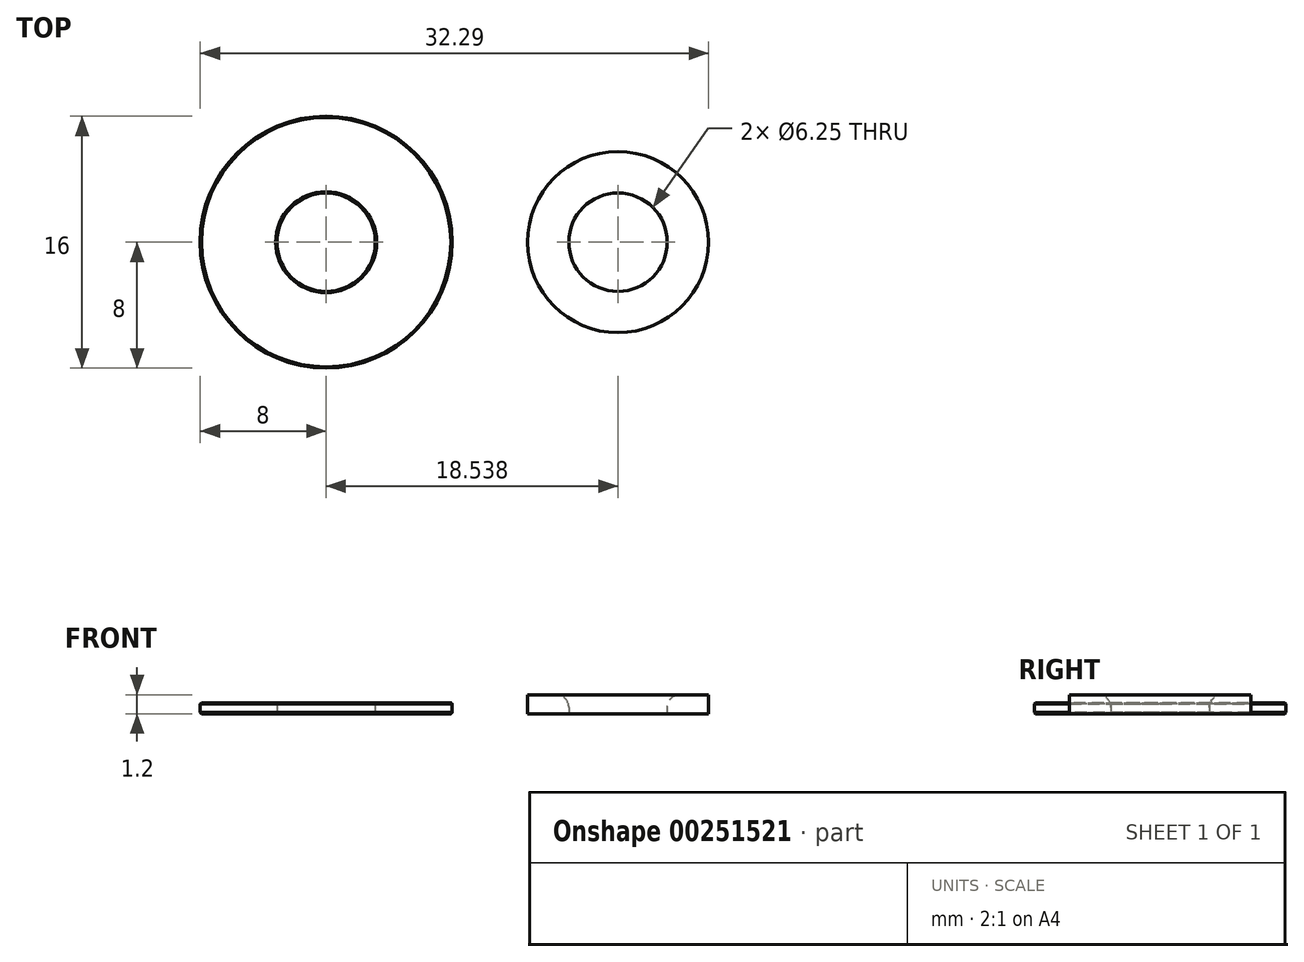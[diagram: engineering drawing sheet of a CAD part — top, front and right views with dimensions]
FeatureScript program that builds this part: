
annotation { "Feature Type Name" : "Feature", "Feature Type Description" : "" }
export const myFeature = defineFeature(function(context is Context, id is Id, definition is map)
    precondition{}
    {
        {
            var Q0;
            Q0=qCreatedBy(makeId("Top.planeOp"),FACE);
            var sketch = newSketch(context, id + "F0", { "sketchPlane" : qUnion([Q0])});
            skCircle(sketch, "E0", {"center": v(0, 0) * mm, "radius": 8 * mm});
            skCircle(sketch, "E1", {"center": v(0, 0) * mm, "radius": 3.12 * mm});
            skCircle(sketch, "E2", {"center": v(18.54, 0) * mm, "radius": 5.75 * mm});
            skCircle(sketch, "E3", {"center": v(18.54, 0) * mm, "radius": 3.12 * mm});
            skSolve(sketch);
        }
        {
            var Q0;
            Q0=makeQuery(id+"F0.imprint","IMPRINT",FACE,{"disambiguationData":[TD([[makeQuery(id+"F0.imprint","IMPRINT",EDGE,{"derivedFrom":sQuery(id+"F0.wireOp",EDGE,"E0")}),1.0]])]});
            extrude(context, id + "F1", {"entities" : qUnion([Q0]), "depth" : .7 * mm});
        }
        {
            var Q0;
            Q0=makeQuery(id+"F1.opExtrude","CAP_EDGE",EDGE,{"disambiguationData":[OSD([sQuery(id+"F0.wireOp",EDGE,"E0")])],"isStart":true});
            var Q1;
            Q1=makeQuery(id+"F1.opExtrude","CAP_EDGE",EDGE,{"disambiguationData":[OSD([sQuery(id+"F0.wireOp",EDGE,"E0")])],"isStart":false});
            var Q2;
            Q2=makeQuery(id+"F1.opExtrude","CAP_EDGE",EDGE,{"disambiguationData":[OSD([sQuery(id+"F0.wireOp",EDGE,"E1")])],"isStart":true});
            var Q3;
            Q3=makeQuery(id+"F1.opExtrude","CAP_EDGE",EDGE,{"disambiguationData":[OSD([sQuery(id+"F0.wireOp",EDGE,"E1")])],"isStart":false});
            chamfer(context, id + "F2", {"entities" : qUnion([Q0, Q1, Q2, Q3]), "width" : 0.08 * mm, "tangentPropagation" : true});
        }
        {
            var Q0;
            Q0=makeQuery(id+"F0.imprint","IMPRINT",FACE,{"disambiguationData":[TD([[makeQuery(id+"F0.imprint","IMPRINT",EDGE,{"derivedFrom":sQuery(id+"F0.wireOp",EDGE,"E2")}),1.0]])]});
            extrude(context, id + "F3", {"entities" : qUnion([Q0]), "depth" : 1.2 * mm});
        }
        {
            var Q0;
            Q0=makeQuery(id+"F3.opExtrude","CAP_EDGE",EDGE,{"disambiguationData":[OSD([sQuery(id+"F0.wireOp",EDGE,"E3")])],"isStart":false});
            fillet(context, id + "F4", {"entities" : qUnion([Q0]), "radius" : 0.8 * mm, "tangentPropagation" : true, "allowEdgeOverflow" : false});
        }
    });
